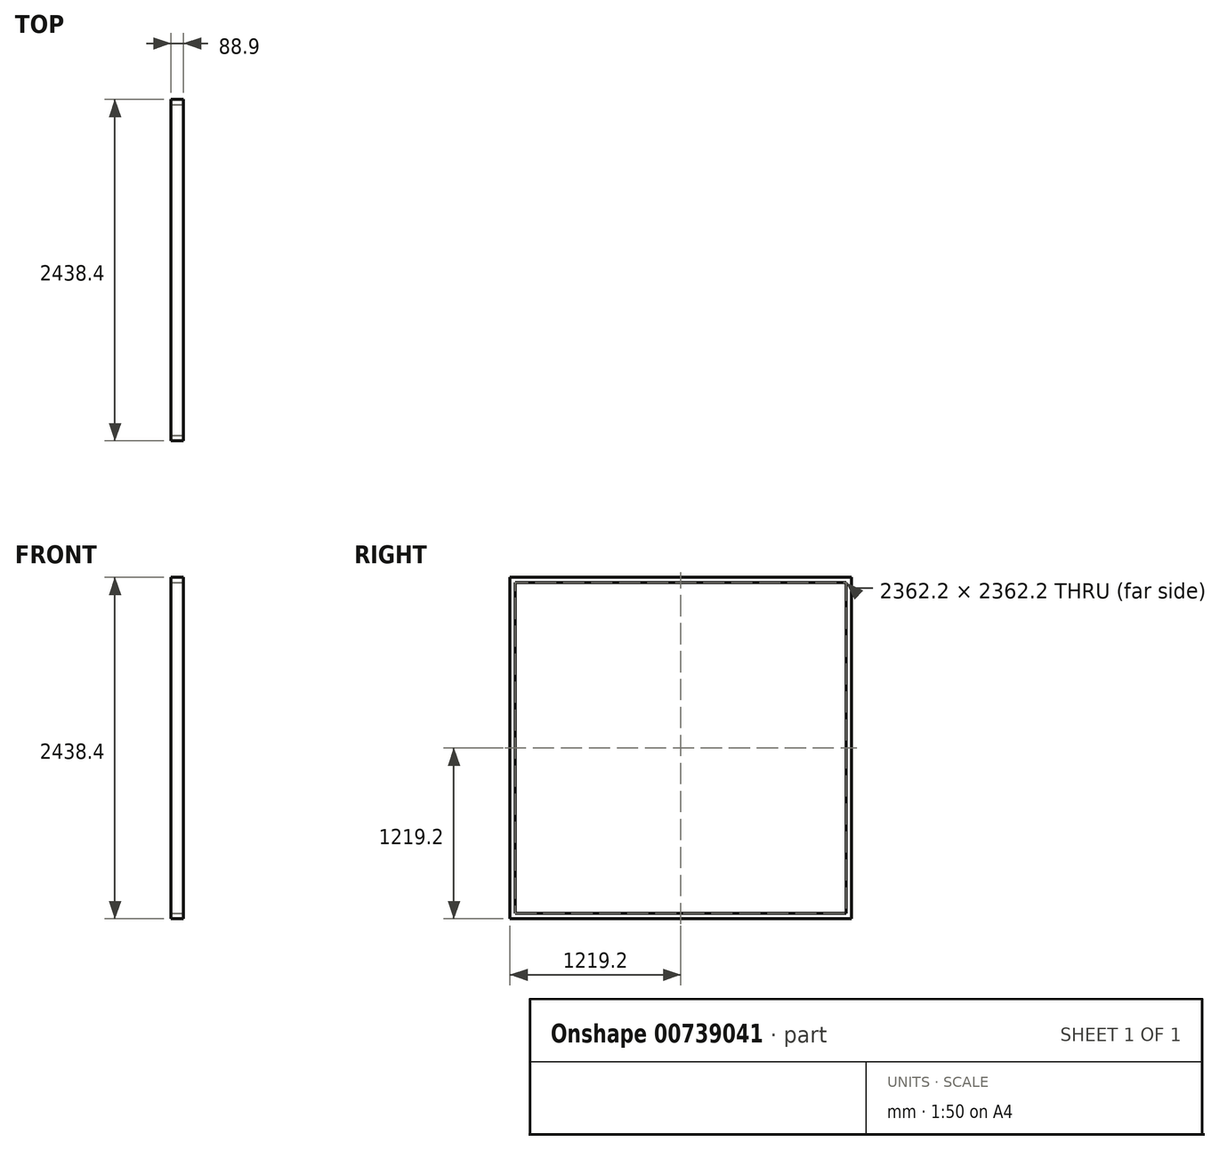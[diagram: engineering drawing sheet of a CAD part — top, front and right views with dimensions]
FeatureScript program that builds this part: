
annotation { "Feature Type Name" : "Feature", "Feature Type Description" : "" }
export const myFeature = defineFeature(function(context is Context, id is Id, definition is map)
    precondition{}
    {
        {
            var Q0;
            Q0=qCreatedBy(makeId("Front.planeOp"),FACE);
            var sketch = newSketch(context, id + "F0", { "sketchPlane" : qUnion([Q0])});
            skLineSegment(sketch, "E0.bottom", {"start": v(-1187.87, 1151.07) * mm, "end": v(1250.53, 1151.07) * mm});
            skLineSegment(sketch, "E0.top", {"start": v(-1187.87, -1287.33) * mm, "end": v(1250.53, -1287.33) * mm});
            skLineSegment(sketch, "E0.left", {"start": v(-1187.87, 1151.07) * mm, "end": v(-1187.87, -1287.33) * mm});
            skLineSegment(sketch, "E0.right", {"start": v(1250.53, 1151.07) * mm, "end": v(1250.53, -1287.33) * mm});
            skLineSegment(sketch, "E1.0", {"start": v(-1149.77, 1112.97) * mm, "end": v(1164.1, 1112.97) * mm});
            skLineSegment(sketch, "E2.0", {"start": v(-1149.77, 1112.97) * mm, "end": v(-1149.77, -1249.23) * mm});
            skLineSegment(sketch, "E2.1", {"start": v(-1149.77, 1112.97) * mm, "end": v(1212.43, 1112.97) * mm});
            skLineSegment(sketch, "E2.2", {"start": v(1212.43, 1112.97) * mm, "end": v(1212.43, -1249.23) * mm});
            skLineSegment(sketch, "E2.3", {"start": v(-1149.77, -1249.23) * mm, "end": v(1212.43, -1249.23) * mm});
            skLineSegment(sketch, "E3.bottom", {"start": v(-787.82, 1112.97) * mm, "end": v(-749.72, 1112.97) * mm});
            skLineSegment(sketch, "E3.top", {"start": v(-787.82, -1249.23) * mm, "end": v(-749.72, -1249.23) * mm});
            skLineSegment(sketch, "E3.left", {"start": v(-787.82, 1112.97) * mm, "end": v(-787.82, -1249.23) * mm});
            skLineSegment(sketch, "E3.right", {"start": v(-749.72, 1112.97) * mm, "end": v(-749.72, -1249.23) * mm});
            skLineSegment(sketch, "E4.bottom", {"start": v(-387.77, 1112.97) * mm, "end": v(-349.67, 1112.97) * mm});
            skLineSegment(sketch, "E4.top", {"start": v(-387.77, -1249.23) * mm, "end": v(-349.67, -1249.23) * mm});
            skLineSegment(sketch, "E4.left", {"start": v(-387.77, 1112.97) * mm, "end": v(-387.77, -1249.23) * mm});
            skLineSegment(sketch, "E4.right", {"start": v(-349.67, 1112.97) * mm, "end": v(-349.67, -1249.23) * mm});
            skLineSegment(sketch, "E5.bottom", {"start": v(12.28, 1112.97) * mm, "end": v(50.38, 1112.97) * mm});
            skLineSegment(sketch, "E5.top", {"start": v(12.28, -1249.23) * mm, "end": v(50.38, -1249.23) * mm});
            skLineSegment(sketch, "E5.left", {"start": v(12.28, 1112.97) * mm, "end": v(12.28, -1249.23) * mm});
            skLineSegment(sketch, "E5.right", {"start": v(50.38, 1112.97) * mm, "end": v(50.38, -1249.23) * mm});
            skLineSegment(sketch, "E6.bottom", {"start": v(450.43, 1112.97) * mm, "end": v(412.33, 1112.97) * mm});
            skLineSegment(sketch, "E6.top", {"start": v(450.43, -1249.23) * mm, "end": v(412.33, -1249.23) * mm});
            skLineSegment(sketch, "E6.left", {"start": v(450.43, 1112.97) * mm, "end": v(450.43, -1249.23) * mm});
            skLineSegment(sketch, "E6.right", {"start": v(412.33, 1112.97) * mm, "end": v(412.33, -1249.23) * mm});
            skLineSegment(sketch, "E7.bottom", {"start": v(812.38, 1112.97) * mm, "end": v(850.48, 1112.97) * mm});
            skLineSegment(sketch, "E7.top", {"start": v(812.38, -1249.23) * mm, "end": v(850.48, -1249.23) * mm});
            skLineSegment(sketch, "E7.left", {"start": v(812.38, 1112.97) * mm, "end": v(812.38, -1249.23) * mm});
            skLineSegment(sketch, "E7.right", {"start": v(850.48, 1112.97) * mm, "end": v(850.48, -1249.23) * mm});
            skLineSegment(sketch, "E8.top", {"start": v(-1187.87, 1189.17) * mm, "end": v(1250.53, 1189.17) * mm});
            skLineSegment(sketch, "E8.left", {"start": v(-1187.87, 1151.07) * mm, "end": v(-1187.87, 1189.17) * mm});
            skLineSegment(sketch, "E8.right", {"start": v(1250.53, 1151.07) * mm, "end": v(1250.53, 1189.17) * mm});
            skSolve(sketch);
        }
        {
            var Q0;
            Q0=makeQuery(id+"F0.imprint","IMPRINT",FACE,{"disambiguationData":[TD([[makeQuery(id+"F0.imprint","IMPRINT",EDGE,{"derivedFrom":sQuery(id+"F0.wireOp",EDGE,"E0.top")}),1.0]])]});
            var Q1;
            Q1=makeQuery(id+"F0.imprint","IMPRINT",FACE,{"disambiguationData":[TD([[makeQuery(id+"F0.imprint","IMPRINT",EDGE,{"derivedFrom":sQuery(id+"F0.wireOp",EDGE,"E7.bottom")}),-1.0]])]});
            var Q2;
            Q2=makeQuery(id+"F0.imprint","IMPRINT",FACE,{"disambiguationData":[TD([[makeQuery(id+"F0.imprint","IMPRINT",EDGE,{"derivedFrom":sQuery(id+"F0.wireOp",EDGE,"E6.bottom")}),1.0]])]});
            var Q3;
            Q3=makeQuery(id+"F0.imprint","IMPRINT",FACE,{"disambiguationData":[TD([[makeQuery(id+"F0.imprint","IMPRINT",EDGE,{"derivedFrom":sQuery(id+"F0.wireOp",EDGE,"E5.bottom")}),-1.0]])]});
            var Q4;
            Q4=makeQuery(id+"F0.imprint","IMPRINT",FACE,{"disambiguationData":[TD([[makeQuery(id+"F0.imprint","IMPRINT",EDGE,{"derivedFrom":sQuery(id+"F0.wireOp",EDGE,"E4.bottom")}),-1.0]])]});
            var Q5;
            Q5=makeQuery(id+"F0.imprint","IMPRINT",FACE,{"disambiguationData":[TD([[makeQuery(id+"F0.imprint","IMPRINT",EDGE,{"derivedFrom":sQuery(id+"F0.wireOp",EDGE,"E3.bottom")}),-1.0]])]});
            var Q6;
            Q6=makeQuery(id+"F0.imprint","IMPRINT",FACE,{"disambiguationData":[TD([[makeQuery(id+"F0.imprint","IMPRINT",EDGE,{"derivedFrom":sQuery(id+"F0.wireOp",EDGE,"E0.bottom")}),1.0]])]});
            extrude(context, id + "F1", {"entities" : qUnion([Q0, Q1, Q2, Q3, Q4, Q5, Q6]), "depth" : 88.9 * mm, "offsetDistance" : 25.4 * mm});
        }
        {
            var Q0;
            Q0=makeQuery(id+"F1.opExtrude","SWEPT_BODY",BODY,{"disambiguationData":[OSD([sQuery(id+"F0.wireOp",EDGE,"E0.top"),sQuery(id+"F0.wireOp",EDGE,"E0.left"),sQuery(id+"F0.wireOp",EDGE,"E0.right"),sQuery(id+"F0.wireOp",EDGE,"E2.0"),sQuery(id+"F0.wireOp",EDGE,"E2.1"),sQuery(id+"F0.wireOp",EDGE,"E2.2"),sQuery(id+"F0.wireOp",EDGE,"E2.3"),sQuery(id+"F0.wireOp",EDGE,"E3.left"),sQuery(id+"F0.wireOp",EDGE,"E3.right"),sQuery(id+"F0.wireOp",EDGE,"E4.left"),sQuery(id+"F0.wireOp",EDGE,"E4.right"),sQuery(id+"F0.wireOp",EDGE,"E5.left"),sQuery(id+"F0.wireOp",EDGE,"E5.right"),sQuery(id+"F0.wireOp",EDGE,"E6.left"),sQuery(id+"F0.wireOp",EDGE,"E6.right"),sQuery(id+"F0.wireOp",EDGE,"E7.left"),sQuery(id+"F0.wireOp",EDGE,"E7.right"),sQuery(id+"F0.wireOp",EDGE,"E8.top"),sQuery(id+"F0.wireOp",EDGE,"E8.left"),sQuery(id+"F0.wireOp",EDGE,"E8.right")])]});
            var Q1;
            Q1=makeQuery(id+"F1.opExtrude","CAP_EDGE",EDGE,{"disambiguationData":[OSD([sQuery(id+"F0.wireOp",EDGE,"E0.right"),sQuery(id+"F0.wireOp",EDGE,"E8.right")])],"isStart":false});
            transform(context, id + "F2", {"entities" : qUnion([Q0]), "transformType" : TransformType.ROTATION, "transformAxis" : qUnion([Q1]), "angle" : 90 * degree, "makeCopy" : false});
        }
    });
